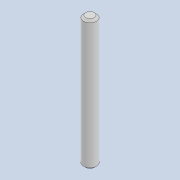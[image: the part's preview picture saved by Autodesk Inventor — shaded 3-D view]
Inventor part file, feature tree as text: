
AUTODESK INVENTOR PART (.ipt)
format: ipt  version: 2020 (Build 240168000, 168)  size: 74,752 bytes
history: native  units: mm
features: extrude x1, chamfer x1, sketch x1
ambient origin geometry x8: Origin, YZ Plane, XZ Plane, XY Plane, X Axis, Y Axis, Z Axis, Center Point
bodies: Solid1 (feature_tree)
feature tree (3):
  extrude  "Extrusion1"  Depth=30.0mm TaperAngle=0.0deg
  chamfer  "Chamfer1"  Distance=0.5mm Angle=45.0deg
  sketch  "Sketch1"  dims[d0=3.0mm d1=30.0mm d2=0.0mm d3=0.5mm d4=2.0mm d5=45.0deg]
